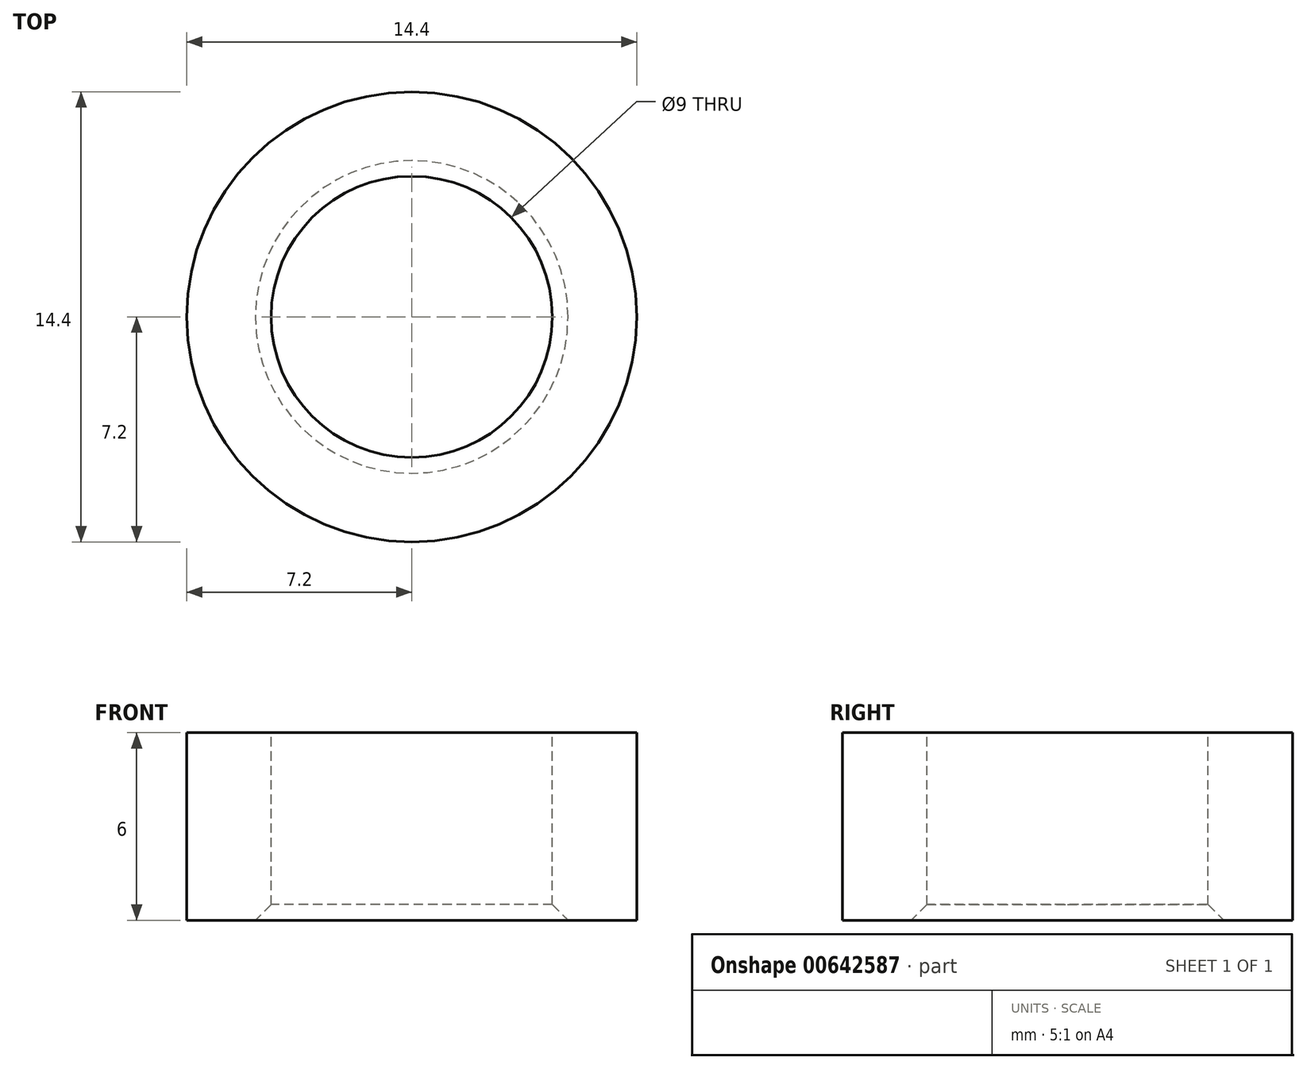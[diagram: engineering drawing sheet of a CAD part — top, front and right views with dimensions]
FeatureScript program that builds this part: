
annotation { "Feature Type Name" : "Feature", "Feature Type Description" : "" }
export const myFeature = defineFeature(function(context is Context, id is Id, definition is map)
    precondition{}
    {
        {
            var Q0;
            Q0=qCreatedBy(makeId("Top.planeOp"),FACE);
            var sketch = newSketch(context, id + "F0", { "sketchPlane" : qUnion([Q0])});
            skCircle(sketch, "E0", {"center": v(0, 0) * mm, "radius": 7.2 * mm});
            skSolve(sketch);
        }
        {
            var Q0;
            Q0 = qSketchRegion(id + "F0", true);
            extrude(context, id + "F1", {"entities" : qUnion([Q0]), "depth" : 6 * mm, "offsetDistance" : 25 * mm});
        }
        {
            var Q0;
            Q0=makeQuery(id+"F1.opExtrude","CAP_FACE",FACE,{"disambiguationData":[OSD([sQuery(id+"F0.wireOp",EDGE,"E0")])],"isStart":false});
            var sketch = newSketch(context, id + "F2", { "sketchPlane" : qUnion([Q0])});
            skCircle(sketch, "E1", {"center": v(0, 0) * mm, "radius": 4.5 * mm});
            skSolve(sketch);
        }
        {
            var Q0;
            Q0=makeQuery(id+"F2.imprint","IMPRINT",FACE,{"disambiguationData":[TD([[makeQuery(id+"F2.imprint","IMPRINT",EDGE,{"derivedFrom":sQuery(id+"F2.wireOp",EDGE,"E1")}),1.0]])]});
            extrude(context, id + "F3", {"entities" : qUnion([Q0]), "operationType" : NewBodyOperationType.REMOVE, "endBound" : BoundingType.THROUGH_ALL, "oppositeDirection" : true, "depth" : 25 * mm, "offsetDistance" : 25 * mm});
        }
        {
            var Q0;
            Q0=makeQuery(id+"F3.boolean.opBoolean","COPY",EDGE,{"derivedFrom":makeQuery(id+"F3.opExtrude","CAP_EDGE",EDGE,{"disambiguationData":[OSD([sQuery(id+"F2.wireOp",EDGE,"E1")])],"isStart":true})});
            var Q1;
            Q1=makeQuery(id+"F3.boolean.opBoolean","INTERSECT",EDGE,{"derivedFrom":[makeQuery(id+"F1.opExtrude","CAP_FACE",FACE,{"disambiguationData":[OSD([sQuery(id+"F0.wireOp",EDGE,"E0")])],"isStart":true}),makeQuery(id+"F3.opExtrude","SWEPT_FACE",FACE,{"disambiguationData":[OSD([sQuery(id+"F2.wireOp",EDGE,"E1")])]})]});
            chamfer(context, id + "F4", {"entities" : qUnion([Q0, Q1]), "chamferType" : ChamferType.OFFSET_ANGLE, "width" : 0.5 * mm, "oppositeDirection" : false, "angle" : 45 * degree, "tangentPropagation" : true});
        }
    });
